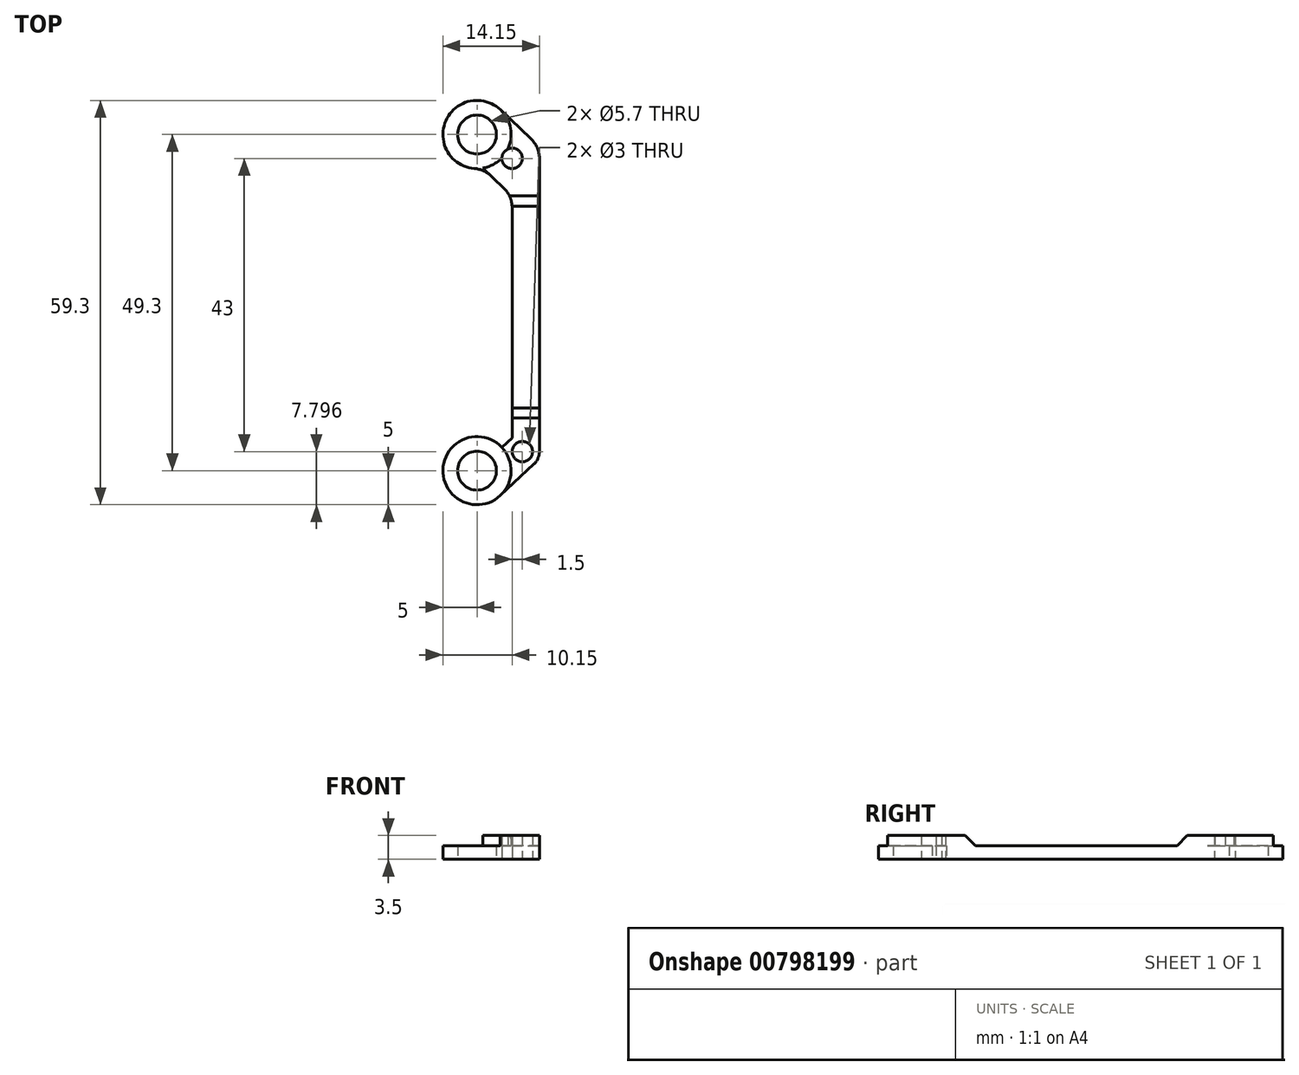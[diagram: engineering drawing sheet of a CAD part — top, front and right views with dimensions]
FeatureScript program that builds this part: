
annotation { "Feature Type Name" : "Feature", "Feature Type Description" : "" }
export const myFeature = defineFeature(function(context is Context, id is Id, definition is map)
    precondition{}
    {
        {
            var Q0;
            Q0=qCreatedBy(makeId("Top.planeOp"),FACE);
            var sketch = newSketch(context, id + "F0", { "sketchPlane" : qUnion([Q0])});
            skLineSegment(sketch, "E0.bottom", {"start": v(14.65, 24.65) * mm, "end": v(-14.65, 24.65) * mm});
            skLineSegment(sketch, "E0.top", {"start": v(14.65, -24.65) * mm, "end": v(-14.65, -24.65) * mm});
            skLineSegment(sketch, "E0.left", {"start": v(14.65, 24.65) * mm, "end": v(14.65, -24.65) * mm});
            skLineSegment(sketch, "E0.right", {"start": v(-14.65, 24.65) * mm, "end": v(-14.65, -24.65) * mm});
            skPoint(sketch, "E0.middle", {"position": v(0, 0) * mm});
            skLineSegment(sketch, "E1.bottom", {"start": v(4.5, 1.35) * mm, "end": v(-4.5, 1.35) * mm});
            skLineSegment(sketch, "E1.top", {"start": v(4.5, -7.65) * mm, "end": v(-4.5, -7.65) * mm});
            skLineSegment(sketch, "E1.left", {"start": v(4.5, 1.35) * mm, "end": v(4.5, -7.65) * mm});
            skLineSegment(sketch, "E1.right", {"start": v(-4.5, 1.35) * mm, "end": v(-4.5, -7.65) * mm});
            skPoint(sketch, "E1.middle", {"position": v(0, -3.15) * mm});
            skSolve(sketch);
        }
        {
            var Q0;
            Q0=qCreatedBy(makeId("Top.planeOp"),FACE);
            var sketch = newSketch(context, id + "F1", { "sketchPlane" : qUnion([Q0])});
            skLineSegment(sketch, "E2.bottom", {"start": v(17.5, 21.15) * mm, "end": v(-17.5, 21.15) * mm});
            skLineSegment(sketch, "E2.top", {"start": v(16, -21.85) * mm, "end": v(-16, -21.85) * mm});
            skLineSegment(sketch, "E2.left", {"start": v(17.5, 21.15) * mm, "end": v(16, -21.85) * mm});
            skLineSegment(sketch, "E2.right", {"start": v(-17.5, 21.15) * mm, "end": v(-16, -21.85) * mm});
            skPoint(sketch, "E2.middle", {"position": v(0, 0) * mm});
            skPoint(sketch, "E3", {"position": v(0, 21.15) * mm});
            skPoint(sketch, "E4", {"position": v(0, -21.85) * mm});
            skSolve(sketch);
        }
        {
            var Q0;
            Q0=qCreatedBy(makeId("Top.planeOp"),FACE);
            var sketch = newSketch(context, id + "F2", { "sketchPlane" : qUnion([Q0])});
            skLineSegment(sketch, "E5.bottom", {"start": v(8.5, 5.35) * mm, "end": v(-8.5, 5.35) * mm, "construction": true});
            skLineSegment(sketch, "E5.top", {"start": v(8.5, -11.65) * mm, "end": v(-8.5, -11.65) * mm, "construction": true});
            skLineSegment(sketch, "E5.left", {"start": v(8.5, 5.35) * mm, "end": v(8.5, -11.65) * mm, "construction": true});
            skLineSegment(sketch, "E5.right", {"start": v(-8.5, 5.35) * mm, "end": v(-8.5, -11.65) * mm, "construction": true});
            skPoint(sketch, "E5.middle", {"position": v(0, -3.15) * mm});
            skCircle(sketch, "E6", {"center": v(-4.5, 1.35) * mm, "radius": 1.1 * mm});
            skCircle(sketch, "E7", {"center": v(4.5, 1.35) * mm, "radius": 1.1 * mm});
            skCircle(sketch, "E8", {"center": v(4.5, -7.65) * mm, "radius": 1.1 * mm});
            skCircle(sketch, "E9", {"center": v(-4.5, -7.65) * mm, "radius": 1.1 * mm});
            skCircle(sketch, "E10", {"center": v(-22.65, -24.65) * mm, "radius": 2.85 * mm});
            skCircle(sketch, "E11", {"center": v(-22.65, -24.65) * mm, "radius": 5 * mm, "construction": true});
            skCircle(sketch, "E12.MirrorC", {"center": v(22.65, -24.65) * mm, "radius": 2.85 * mm});
            skCircle(sketch, "E13.MirrorC", {"center": v(22.65, -24.65) * mm, "radius": 5 * mm, "construction": true});
            skCircle(sketch, "E14.MirrorC", {"center": v(22.65, 24.65) * mm, "radius": 2.85 * mm});
            skCircle(sketch, "E15.MirrorC", {"center": v(22.65, 24.65) * mm, "radius": 5 * mm, "construction": true});
            skCircle(sketch, "E16.MirrorC", {"center": v(-22.65, 24.65) * mm, "radius": 2.85 * mm});
            skCircle(sketch, "E17.MirrorC", {"center": v(-22.65, 24.65) * mm, "radius": 5 * mm, "construction": true});
            skLineSegment(sketch, "E18", {"start": v(-22.65, 24.65) * mm, "end": v(-8.5, 5.35) * mm, "construction": true});
            skLineSegment(sketch, "E19", {"start": v(8.5, 5.35) * mm, "end": v(22.65, 24.65) * mm, "construction": true});
            skLineSegment(sketch, "E20", {"start": v(8.5, -11.65) * mm, "end": v(22.65, -24.65) * mm, "construction": true});
            skLineSegment(sketch, "E21", {"start": v(-8.5, -11.65) * mm, "end": v(-22.65, -24.65) * mm, "construction": true});
            skLineSegment(sketch, "E22", {"start": v(-21.73, -19.73) * mm, "end": v(-8.5, -7.58) * mm});
            skLineSegment(sketch, "E23", {"start": v(-17.67, -24.15) * mm, "end": v(-4.07, -11.65) * mm});
            skLineSegment(sketch, "E24", {"start": v(-22.7, 19.65) * mm, "end": v(-8.5, 0.28) * mm});
            skLineSegment(sketch, "E25", {"start": v(-4.78, 5.35) * mm, "end": v(-17.87, 23.2) * mm});
            skLineSegment(sketch, "E26", {"start": v(-14.9, 9) * mm, "end": v(-10.06, 12.55) * mm, "construction": true});
            skLineSegment(sketch, "E27", {"start": v(-8.74, -15.94) * mm, "end": v(-12.8, -11.52) * mm, "construction": true});
            skPoint(sketch, "E28", {"position": v(-12.48, 10.78) * mm});
            skPoint(sketch, "E29", {"position": v(-10.77, -13.73) * mm});
            skLineSegment(sketch, "E30.MirrorCS", {"start": v(17.67, -24.15) * mm, "end": v(4.07, -11.65) * mm});
            skLineSegment(sketch, "E31.MirrorCS", {"start": v(21.73, -19.73) * mm, "end": v(8.5, -7.58) * mm});
            skLineSegment(sketch, "E32.MirrorCS", {"start": v(22.7, 19.65) * mm, "end": v(8.5, 0.28) * mm});
            skLineSegment(sketch, "E33.MirrorCS", {"start": v(4.78, 5.35) * mm, "end": v(17.87, 23.2) * mm});
            skLineSegment(sketch, "E34", {"start": v(-4.78, 5.35) * mm, "end": v(4.78, 5.35) * mm});
            skLineSegment(sketch, "E35", {"start": v(8.5, 0.28) * mm, "end": v(8.5, -7.58) * mm});
            skLineSegment(sketch, "E36", {"start": v(4.07, -11.65) * mm, "end": v(-4.07, -11.65) * mm});
            skLineSegment(sketch, "E37", {"start": v(-8.5, -7.58) * mm, "end": v(-8.5, 0.28) * mm});
            skArc(sketch, "E38", {"start": v(-17.67, -24.15) * mm, "mid": v(-26.33, -28.03) * mm, "end": v(-21.73, -19.73) * mm});
            skArc(sketch, "E39", {"start": v(21.73, -19.73) * mm, "mid": v(26.33, -28.03) * mm, "end": v(17.67, -24.15) * mm});
            skArc(sketch, "E40", {"start": v(22.7, 19.65) * mm, "mid": v(25.6, 28.68) * mm, "end": v(17.87, 23.2) * mm});
            skArc(sketch, "E41", {"start": v(-17.87, 23.2) * mm, "mid": v(-25.6, 28.68) * mm, "end": v(-22.7, 19.65) * mm});
            skSolve(sketch);
        }
        {
            var Q0;
            Q0=qCreatedBy(makeId("Top.planeOp"),FACE);
            var sketch = newSketch(context, id + "F3", { "sketchPlane" : qUnion([Q0])});
            skCircle(sketch, "E42", {"center": v(-22.65, 24.65) * mm, "radius": 2.85 * mm});
            skCircle(sketch, "E43", {"center": v(-17.5, 21.15) * mm, "radius": 1.5 * mm});
            skCircle(sketch, "E44", {"center": v(-22.65, -24.65) * mm, "radius": 2.85 * mm});
            skCircle(sketch, "E45", {"center": v(-16, -21.85) * mm, "radius": 1.5 * mm});
            skArc(sketch, "E46", {"start": v(-21.81, 19.72) * mm, "mid": v(-27.43, 26.1) * mm, "end": v(-19.21, 28.28) * mm});
            skArc(sketch, "E47", {"start": v(-19.23, -28.3) * mm, "mid": v(-27.65, -24.48) * mm, "end": v(-19, -21.23) * mm});
            skArc(sketch, "E48", {"start": v(-14.75, 24.05) * mm, "mid": v(-13.83, 22.73) * mm, "end": v(-13.5, 21.15) * mm});
            skArc(sketch, "E49", {"start": v(-14.3, -23.68) * mm, "mid": v(-13.7, -22.85) * mm, "end": v(-13.5, -21.85) * mm});
            skLineSegment(sketch, "E50", {"start": v(-19.23, -28.3) * mm, "end": v(-14.3, -23.68) * mm});
            skLineSegment(sketch, "E51", {"start": v(-14.75, 24.05) * mm, "end": v(-19.21, 28.28) * mm});
            skLineSegment(sketch, "E52", {"start": v(-13.5, 21.15) * mm, "end": v(-13.5, -21.85) * mm});
            skLineSegment(sketch, "E53", {"start": v(-17.5, 15.63) * mm, "end": v(-17.5, -19.83) * mm});
            skLineSegment(sketch, "E54", {"start": v(-17.5, -19.83) * mm, "end": v(-19, -21.23) * mm});
            skLineSegment(sketch, "E55", {"start": v(-17.5, 15.63) * mm, "end": v(-21.81, 19.72) * mm});
            skLineSegment(sketch, "E56", {"start": v(-20.25, 18.24) * mm, "end": v(-14.75, 24.05) * mm, "construction": true});
            skLineSegment(sketch, "E57", {"start": v(-14.3, -23.68) * mm, "end": v(-17.7, -20.03) * mm, "construction": true});
            skSolve(sketch);
        }
        {
            var Q0;
            Q0 = qSketchRegion(id + "F3", true);
            extrude(context, id + "F4", {"entities" : qUnion([Q0]), "depth" : 2 * mm, "offsetDistance" : 25 * mm});
        }
        {
            var Q0;
            Q0=makeQuery(id+"F4.opExtrude","CAP_FACE",FACE,{"disambiguationData":[OSD([sQuery(id+"F3.wireOp",EDGE,"E42"),sQuery(id+"F3.wireOp",EDGE,"E43"),sQuery(id+"F3.wireOp",EDGE,"E44"),sQuery(id+"F3.wireOp",EDGE,"E45"),sQuery(id+"F3.wireOp",EDGE,"E46"),sQuery(id+"F3.wireOp",EDGE,"E47"),sQuery(id+"F3.wireOp",EDGE,"E48"),sQuery(id+"F3.wireOp",EDGE,"E49"),sQuery(id+"F3.wireOp",EDGE,"E50"),sQuery(id+"F3.wireOp",EDGE,"E51"),sQuery(id+"F3.wireOp",EDGE,"E52"),sQuery(id+"F3.wireOp",EDGE,"E53"),sQuery(id+"F3.wireOp",EDGE,"E54"),sQuery(id+"F3.wireOp",EDGE,"E55")])],"isStart":false});
            var sketch = newSketch(context, id + "F5", { "sketchPlane" : qUnion([Q0])});
            skArc(sketch, "E58", {"start": v(-21.81, 19.72) * mm, "mid": v(-20.28, 20.25) * mm, "end": v(-19, 21.24) * mm});
            skArc(sketch, "E59", {"start": v(-18.13, 22.5) * mm, "mid": v(-17.73, 25.57) * mm, "end": v(-19.21, 28.28) * mm});
            skLineSegment(sketch, "E60", {"start": v(-21.81, 19.72) * mm, "end": v(-17.5, 15.63) * mm});
            skLineSegment(sketch, "E61", {"start": v(-17.5, 15.63) * mm, "end": v(-13.5, 15.63) * mm});
            skLineSegment(sketch, "E62", {"start": v(-13.5, 15.63) * mm, "end": v(-13.5, 21.15) * mm});
            skLineSegment(sketch, "E63", {"start": v(-19.21, 28.28) * mm, "end": v(-14.75, 24.05) * mm});
            skArc(sketch, "E64", {"start": v(-14.75, 24.05) * mm, "mid": v(-13.83, 22.73) * mm, "end": v(-13.5, 21.15) * mm});
            skArc(sketch, "E65", {"start": v(-21.3, -19.83) * mm, "mid": v(-20.04, -20.38) * mm, "end": v(-18.98, -21.25) * mm});
            skArc(sketch, "E66", {"start": v(-19.23, -28.3) * mm, "mid": v(-17.8, -23.46) * mm, "end": v(-21.3, -19.83) * mm});
            skLineSegment(sketch, "E67", {"start": v(-17.5, -16.94) * mm, "end": v(-13.5, -16.94) * mm});
            skLineSegment(sketch, "E68", {"start": v(-13.5, -16.94) * mm, "end": v(-13.5, -21.85) * mm});
            skLineSegment(sketch, "E69", {"start": v(-19.23, -28.3) * mm, "end": v(-14.3, -23.68) * mm});
            skArc(sketch, "E70", {"start": v(-14.3, -23.68) * mm, "mid": v(-13.7, -22.85) * mm, "end": v(-13.5, -21.85) * mm});
            skLineSegment(sketch, "E71", {"start": v(-17.5, -16.94) * mm, "end": v(-17.5, -13.26) * mm, "construction": true});
            skArc(sketch, "E72", {"start": v(-17.5, -16.94) * mm, "mid": v(-18.69, -19.33) * mm, "end": v(-21.3, -19.83) * mm});
            skSolve(sketch);
        }
        {
            var Q0;
            {var subQ1=sQuery(id+"F5.wireOp",EDGE,"E58");Q0=makeQuery(id+"F5.imprint","IMPRINT",FACE,{"disambiguationData":[TD([[makeQuery(id+"F5.imprint","IMPRINT",EDGE,{"derivedFrom":subQ1}),-1.0]])]});}
            var Q1;
            {var subQ0=sQuery(id+"F5.wireOp",EDGE,"E67");Q1=makeQuery(id+"F5.imprint","IMPRINT",FACE,{"disambiguationData":[TD([[makeQuery(id+"F5.imprint","IMPRINT",EDGE,{"derivedFrom":subQ0}),-1.0]])]});}
            var Q2;
            {var subQ2=sQuery(id+"F5.wireOp",EDGE,"E72");Q2=makeQuery(id+"F5.imprint","IMPRINT",FACE,{"disambiguationData":[TD([[makeQuery(id+"F5.imprint","IMPRINT",EDGE,{"derivedFrom":subQ2}),1.0]])]});}
            var Q3;
            Q3=makeQuery(id+"F4.opExtrude","CAP_FACE",FACE,{"disambiguationData":[OSD([sQuery(id+"F3.wireOp",EDGE,"E42"),sQuery(id+"F3.wireOp",EDGE,"E43"),sQuery(id+"F3.wireOp",EDGE,"E44"),sQuery(id+"F3.wireOp",EDGE,"E45"),sQuery(id+"F3.wireOp",EDGE,"E46"),sQuery(id+"F3.wireOp",EDGE,"E47"),sQuery(id+"F3.wireOp",EDGE,"E48"),sQuery(id+"F3.wireOp",EDGE,"E49"),sQuery(id+"F3.wireOp",EDGE,"E50"),sQuery(id+"F3.wireOp",EDGE,"E51"),sQuery(id+"F3.wireOp",EDGE,"E52"),sQuery(id+"F3.wireOp",EDGE,"E53"),sQuery(id+"F3.wireOp",EDGE,"E54"),sQuery(id+"F3.wireOp",EDGE,"E55")])],"isStart":true});
            extrude(context, id + "F6", {"entities" : qUnion([Q0, Q1, Q2]), "operationType" : NewBodyOperationType.ADD, "depth" : 1.5 * mm, "offsetDistance" : 25 * mm, "hasSecondDirection" : true, "secondDirectionBound" : SecondDirectionBoundingType.UP_TO_SURFACE, "secondDirectionOppositeDirection" : true, "secondDirectionDepth" : 25 * mm, "secondDirectionBoundEntityFace" : qUnion([Q3])});
        }
        {
            var Q0;
            Q0=makeQuery(id+"F6.boolean.opBoolean","INTERSECT",EDGE,{"derivedFrom":[makeQuery(id+"F4.opExtrude","CAP_FACE",FACE,{"disambiguationData":[OSD([sQuery(id+"F3.wireOp",EDGE,"E42"),sQuery(id+"F3.wireOp",EDGE,"E43"),sQuery(id+"F3.wireOp",EDGE,"E44"),sQuery(id+"F3.wireOp",EDGE,"E45"),sQuery(id+"F3.wireOp",EDGE,"E46"),sQuery(id+"F3.wireOp",EDGE,"E47"),sQuery(id+"F3.wireOp",EDGE,"E48"),sQuery(id+"F3.wireOp",EDGE,"E49"),sQuery(id+"F3.wireOp",EDGE,"E50"),sQuery(id+"F3.wireOp",EDGE,"E51"),sQuery(id+"F3.wireOp",EDGE,"E52"),sQuery(id+"F3.wireOp",EDGE,"E53"),sQuery(id+"F3.wireOp",EDGE,"E54"),sQuery(id+"F3.wireOp",EDGE,"E55")])],"isStart":false}),makeQuery(id+"F6.opExtrude","SWEPT_FACE",FACE,{"disambiguationData":[OSD([sQuery(id+"F5.wireOp",EDGE,"E67")])]})]});
            var Q1;
            Q1=makeQuery(id+"F6.boolean.opBoolean","INTERSECT",EDGE,{"derivedFrom":[makeQuery(id+"F4.opExtrude","CAP_FACE",FACE,{"disambiguationData":[OSD([sQuery(id+"F3.wireOp",EDGE,"E42"),sQuery(id+"F3.wireOp",EDGE,"E43"),sQuery(id+"F3.wireOp",EDGE,"E44"),sQuery(id+"F3.wireOp",EDGE,"E45"),sQuery(id+"F3.wireOp",EDGE,"E46"),sQuery(id+"F3.wireOp",EDGE,"E47"),sQuery(id+"F3.wireOp",EDGE,"E48"),sQuery(id+"F3.wireOp",EDGE,"E49"),sQuery(id+"F3.wireOp",EDGE,"E50"),sQuery(id+"F3.wireOp",EDGE,"E51"),sQuery(id+"F3.wireOp",EDGE,"E52"),sQuery(id+"F3.wireOp",EDGE,"E53"),sQuery(id+"F3.wireOp",EDGE,"E54"),sQuery(id+"F3.wireOp",EDGE,"E55")])],"isStart":false}),makeQuery(id+"F6.opExtrude","SWEPT_FACE",FACE,{"disambiguationData":[OSD([sQuery(id+"F5.wireOp",EDGE,"E61")])]})]});
            chamfer(context, id + "F7", {"entities" : qUnion([Q0, Q1]), "width" : 1.5 * mm, "tangentPropagation" : true});
        }
        {
            var Q0;
            Q0=makeQuery(id+"F4.opExtrude","SWEPT_EDGE",EDGE,{"disambiguationData":[OSD([sQuery(id+"F3.wireOp",EDGE,"E53"),sQuery(id+"F3.wireOp",EDGE,"E55")])]});
            var Q1;
            Q1=makeQuery(id+"F4.opExtrude","SWEPT_EDGE",EDGE,{"disambiguationData":[OSD([sQuery(id+"F3.wireOp",EDGE,"E46"),sQuery(id+"F3.wireOp",EDGE,"E55")])]});
            fillet(context, id + "F8", {"entities" : qUnion([Q0, Q1]), "radius" : 4 * mm, "tangentPropagation" : true, "defaultsChanged" : false, "vertexSettings" : [], "allowEdgeOverflow" : false});
        }
    });
